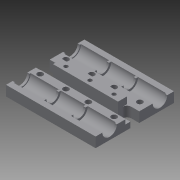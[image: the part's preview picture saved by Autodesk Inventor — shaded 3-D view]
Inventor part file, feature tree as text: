
AUTODESK INVENTOR PART (.ipt)
format: ipt  version: 2014 SP1 (Build 180222100, 222)  size: 344,576 bytes
history: native  units: mm
features: sketch x20, extrude x19, plane x2, hole x1
ambient origin geometry x8: Origin, YZ Plane, XZ Plane, XY Plane, X Axis, Y Axis, Z Axis, Center Point
bodies: Body1 (feature_tree)
feature tree (42):
  extrude  "Extrusion4"  Depth=70.0mm
  extrude  "Extrusion5"  Depth=21.0mm
  extrude  "Extrusion6"  Depth=10.0mm
  extrude  "Extrusion7"  Depth=11.5mm
  extrude  "Extrusion8"  Depth=23.0mm
  extrude  "Extrusion9"  Depth=11.5mm
  extrude  "Extrusion10"  Depth=5.0mm
  plane  "Work Plane1"
  extrude  "Extrusion11"  Depth=5.0mm
  plane  "Work Plane4"
  extrude  "Extrusion13"  Depth=5.0mm
  extrude  "Extrusion14"  Depth=5.0mm
  extrude  "Extrusion15"  Depth=22.5mm
  extrude  "Extrusion16"  Depth=15.0mm
  hole  "Hole2"  [1 undecoded]
  extrude  "Extrusion17"  Depth=2.0mm TaperAngle=0.0deg
  extrude  "Extrusion19"  Depth=2.0mm TaperAngle=0.0deg
  extrude  "Extrusion21"  Depth=2.0mm TaperAngle=0.0deg
  extrude  "Extrusion25"  Depth=2.0mm TaperAngle=0.0deg
  extrude  "Extrusion26"  Depth=11.0mm
  extrude  "Extrusion27"  Depth=2.0mm TaperAngle=0.0deg
  extrude  "Extrusion28"  Depth=2.0mm TaperAngle=0.0deg
  sketch  "Sketch1"  dims[d0=80.0mm d1=70.0mm]
  sketch  "Sketch4"  dims[d2=21.0mm d3=21.0mm]
  sketch  "Sketch5"  dims[d39=10.0mm d40=10.0mm]
  sketch  "Sketch7"  dims[d41=23.0mm d42=11.5mm]
  sketch  "Sketch8"  dims[d43=66.0mm d44=23.0mm]
  sketch  "Sketch9"  dims[d45=66.0mm d46=11.5mm]
  sketch  "Sketch10"  dims[d47=5.0mm d48=5.0mm]
  sketch  "Sketch11"  dims[d49=5.0mm d50=5.0mm]
  sketch  "Sketch14"  dims[d51=5.0mm d52=5.0mm]
  sketch  "Sketch15"  dims[d53=5.0mm d54=5.0mm]
  sketch  "Sketch16"  dims[d55=14.0mm d56=0.0mm d57=22.5mm]
  sketch  "Sketch17"  dims[d58=45.0mm d59=15.0mm]
  sketch  "Sketch18"  dims[d60=10.0mm d61=0.0mm d62=15.0mm]
  sketch  "Sketch19"  dims[d63=10.0mm d64=0.0mm d72=2.0mm d73=0.0mm]
  sketch  "Sketch21"  dims[d74=13.0mm d75=2.0mm d76=0.0mm]
  sketch  "Sketch23"  dims[d77=13.0mm d78=2.0mm d79=0.0mm]
  sketch  "Sketch25"  dims[d80=13.0mm d81=2.0mm d82=0.0mm]
  sketch  "Sketch27"  dims[d83=-29.0mm d84=11.0mm]
  sketch  "Sketch28"  dims[d85=2.0mm d86=2.0mm d87=0.0mm]
  sketch  "Sketch29"  dims[d93=-27.0mm d97=2.0mm d98=0.0mm d99=11.0mm d100=15.0mm d101=2.0mm d102=0.0mm d103=11.0mm d104=15.0mm d105=2.0mm d106=0.0mm d107=10.0mm d108=0.0mm d109=3.5mm d110=6.0mm d111=6.0mm d112=4.0mm d113=90.0deg d114=8.0mm d115=20.594885mm d116=6.0mm d117=3.0mm d118=0.0mm d122=6.0mm d123=3.0mm d124=0.0mm d128=6.0mm d129=3.0mm d130=0.0mm d143=10.0mm d144=0.0mm d146=10.0mm d147=0.0mm d148=4.0mm d149=0.0mm d150=6.0mm d151=0.0mm]
note: 1 required parameter value undecoded (feature->parameter linkage not recoverable at this tier; creation-order binding heuristic only, values carry confidence <= 0.55)
